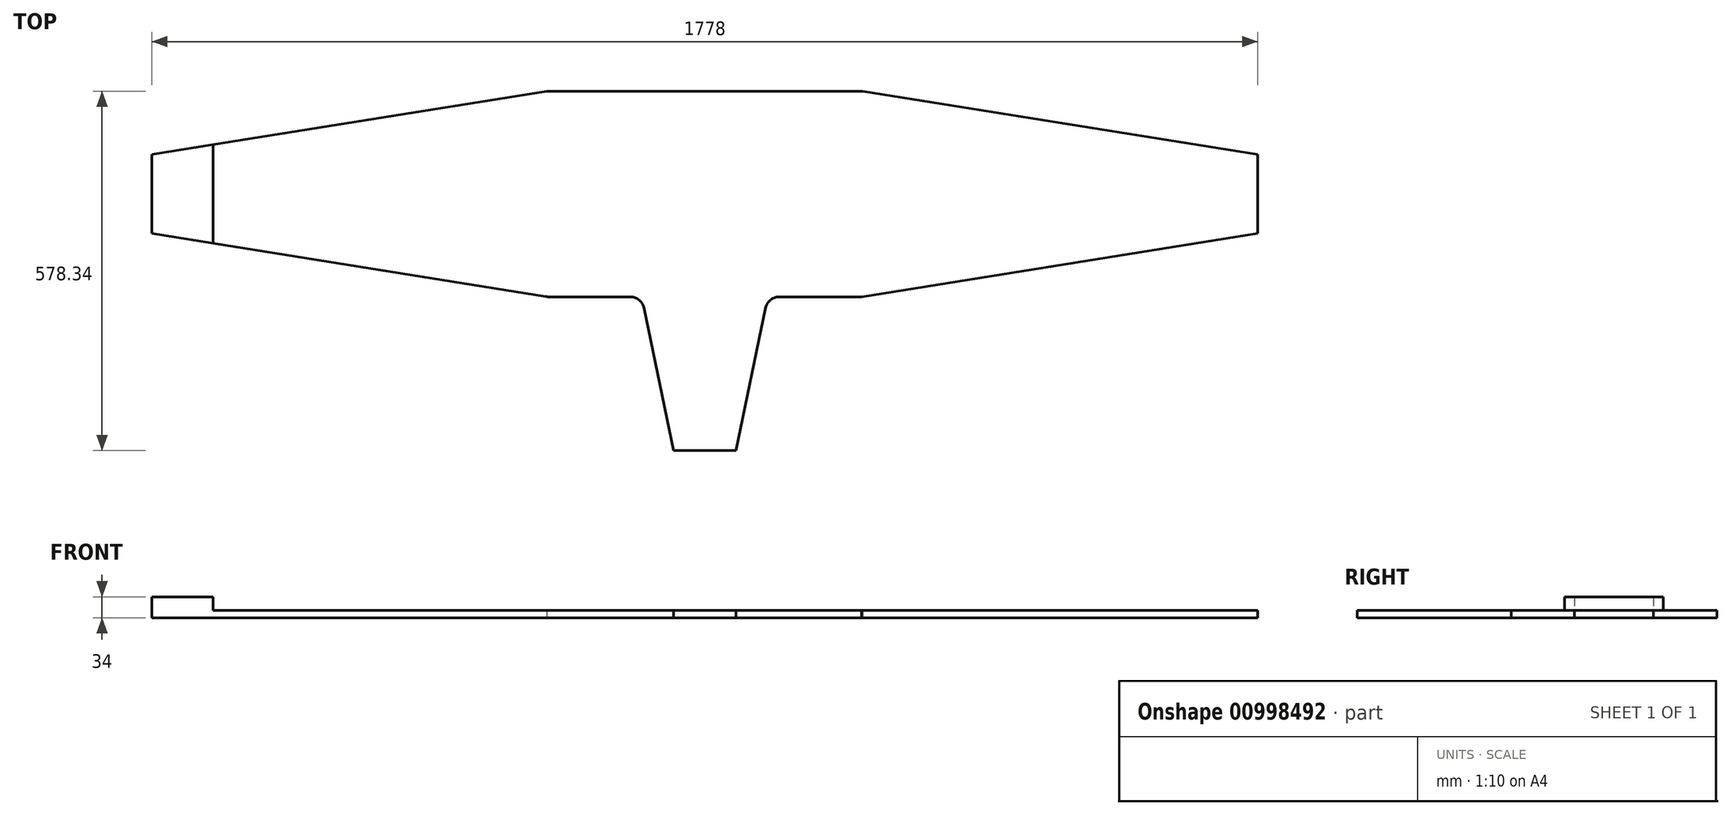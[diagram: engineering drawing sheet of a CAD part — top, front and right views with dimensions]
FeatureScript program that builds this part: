
annotation { "Feature Type Name" : "Feature", "Feature Type Description" : "" }
export const myFeature = defineFeature(function(context is Context, id is Id, definition is map)
    precondition{}
    {
        {
            var Q0;
            Q0=qCreatedBy(makeId("Top.planeOp"),FACE);
            var sketch = newSketch(context, id + "F0", { "sketchPlane" : qUnion([Q0])});
            skLineSegment(sketch, "E0.bottom", {"start": v(-254, 165.46) * mm, "end": v(0, 165.46) * mm});
            skLineSegment(sketch, "E0.top", {"start": v(-248.77, -165.46) * mm, "end": v(-119.54, -165.46) * mm});
            skLineSegment(sketch, "E0.right", {"start": v(0, 165.46) * mm, "end": v(0, -165.46) * mm});
            skLineSegment(sketch, "E1.bottom", {"start": v(-254, 165.46) * mm, "end": v(-889, 63.5) * mm});
            skLineSegment(sketch, "E1.top", {"start": v(-255.73, -164.9) * mm, "end": v(-889, -63.5) * mm});
            skLineSegment(sketch, "E1.right", {"start": v(-889, 63.5) * mm, "end": v(-889, -63.5) * mm});
            skLineSegment(sketch, "E2.top", {"start": v(0, -412.88) * mm, "end": v(-50.17, -412.88) * mm});
            skLineSegment(sketch, "E2.left", {"start": v(0, -165.46) * mm, "end": v(0, -412.88) * mm});
            skLineSegment(sketch, "E2.right", {"start": v(-98, -182.98) * mm, "end": v(-50.17, -412.88) * mm});
            skLineSegment(sketch, "E3.MirrorCS", {"start": v(252.27, -165.46) * mm, "end": v(889, -63.5) * mm});
            skLineSegment(sketch, "E4.MirrorCS", {"start": v(252.27, -165.46) * mm, "end": v(119.54, -165.46) * mm});
            skLineSegment(sketch, "E5.MirrorCS", {"start": v(254, 165.46) * mm, "end": v(889, 63.5) * mm});
            skLineSegment(sketch, "E6.MirrorCS", {"start": v(254, 165.46) * mm, "end": v(0, 165.46) * mm});
            skLineSegment(sketch, "E7.MirrorCS", {"start": v(98, -182.98) * mm, "end": v(50.17, -412.88) * mm});
            skLineSegment(sketch, "E8.MirrorCS", {"start": v(0, -412.88) * mm, "end": v(50.17, -412.88) * mm});
            skLineSegment(sketch, "E9.MirrorCS", {"start": v(889, 63.5) * mm, "end": v(889, -63.5) * mm});
            skPoint(sketch, "E10.visualSharp", {"position": v(-101.65, -165.46) * mm});
            skArc(sketch, "E10.filletArc", {"start": v(-98, -182.98) * mm, "mid": v(-105.66, -170.4) * mm, "end": v(-119.54, -165.46) * mm});
            skPoint(sketch, "E11.visualSharp", {"position": v(101.65, -165.46) * mm});
            skArc(sketch, "E11.filletArc", {"start": v(119.54, -165.46) * mm, "mid": v(105.66, -170.4) * mm, "end": v(98, -182.98) * mm});
            skPoint(sketch, "E12.visualSharp", {"position": v(-252.27, -165.46) * mm});
            skArc(sketch, "E12.filletArc", {"start": v(-255.73, -164.9) * mm, "mid": v(-252.26, -165.32) * mm, "end": v(-248.77, -165.46) * mm});
            skSolve(sketch);
        }
        {
            var Q0;
            Q0 = qSketchRegion(id + "F0", true);
            extrude(context, id + "F1", {"entities" : qUnion([Q0]), "depth" : 12 * mm, "offsetDistance" : 25.4 * mm});
        }
        {
            var Q0;
            Q0=makeQuery(id+"F1.opExtrude","CAP_FACE",FACE,{"disambiguationData":[OSD([sQuery(id+"F0.wireOp",EDGE,"E0.bottom"),sQuery(id+"F0.wireOp",EDGE,"E0.top"),sQuery(id+"F0.wireOp",EDGE,"E1.bottom"),sQuery(id+"F0.wireOp",EDGE,"E1.top"),sQuery(id+"F0.wireOp",EDGE,"E1.right"),sQuery(id+"F0.wireOp",EDGE,"E2.top"),sQuery(id+"F0.wireOp",EDGE,"E2.right"),sQuery(id+"F0.wireOp",EDGE,"E3.MirrorCS"),sQuery(id+"F0.wireOp",EDGE,"E4.MirrorCS"),sQuery(id+"F0.wireOp",EDGE,"E5.MirrorCS"),sQuery(id+"F0.wireOp",EDGE,"E6.MirrorCS"),sQuery(id+"F0.wireOp",EDGE,"E7.MirrorCS"),sQuery(id+"F0.wireOp",EDGE,"E8.MirrorCS"),sQuery(id+"F0.wireOp",EDGE,"E9.MirrorCS")])],"isStart":false});
            var sketch = newSketch(context, id + "F2", { "sketchPlane" : qUnion([Q0])});
            skLineSegment(sketch, "E13", {"start": v(-790.66, -79.25) * mm, "end": v(-790.66, 79.3) * mm});
            skSolve(sketch);
        }
        {
            var Q0;
            {var subQ0=sQuery(id+"F2.wireOp",EDGE,"E13");Q0=makeQuery(id+"F2.imprint","IMPRINT",FACE,{"disambiguationData":[TD([[makeQuery(id+"F2.imprint","IMPRINT",EDGE,{"derivedFrom":subQ0}),1.0]])]});}
            extrude(context, id + "F3", {"entities" : qUnion([Q0]), "operationType" : NewBodyOperationType.ADD, "depth" : 22 * mm, "offsetDistance" : 25.4 * mm});
        }
    });
